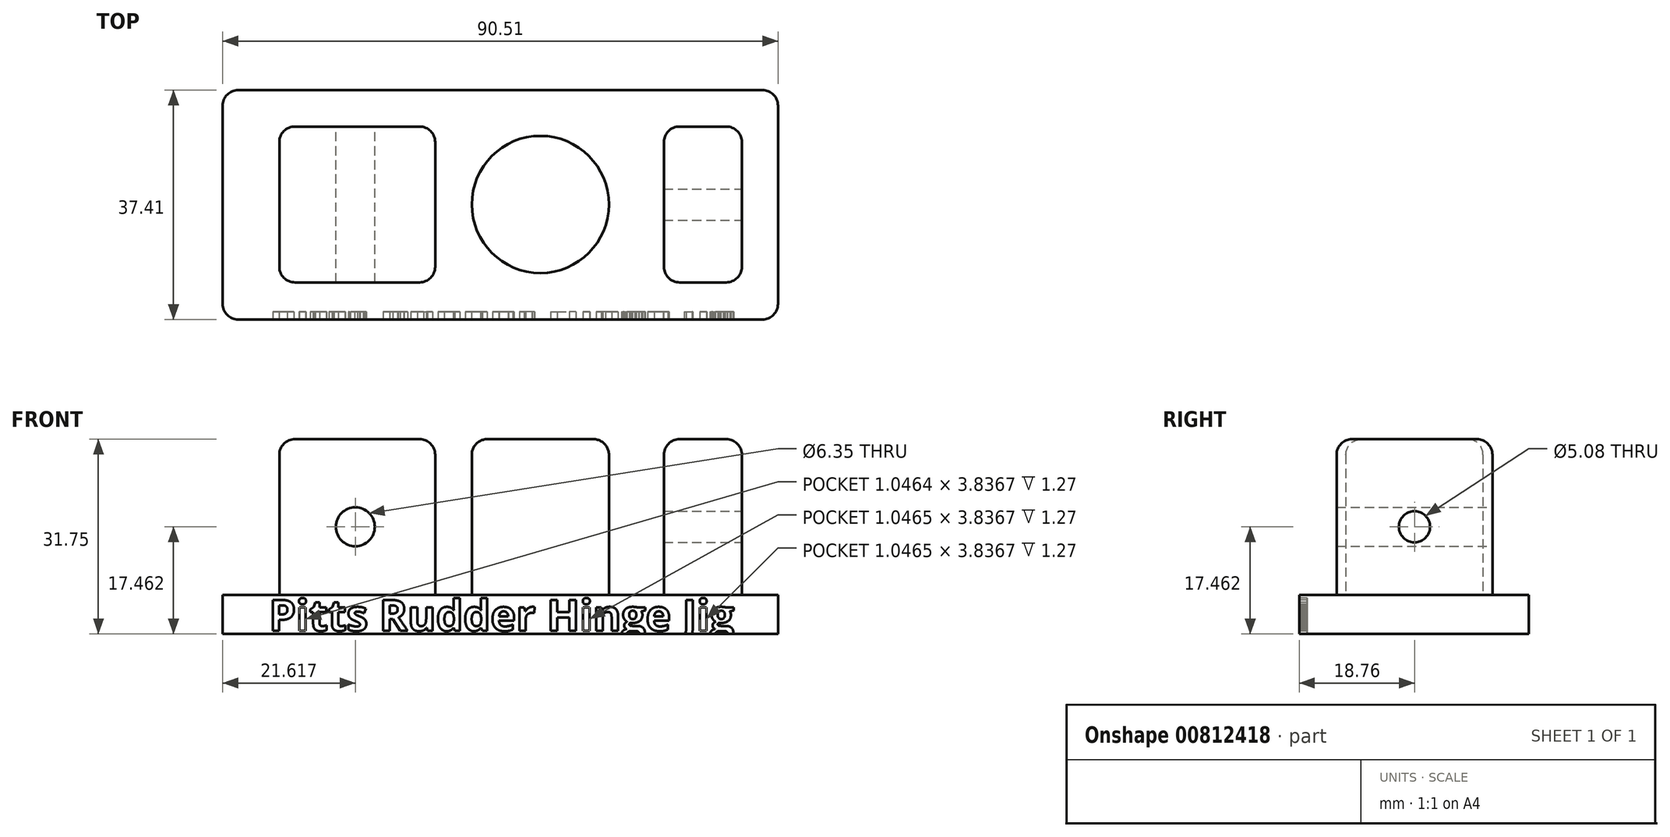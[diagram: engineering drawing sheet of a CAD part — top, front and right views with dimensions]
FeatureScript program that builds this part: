
annotation { "Feature Type Name" : "Feature", "Feature Type Description" : "" }
export const myFeature = defineFeature(function(context is Context, id is Id, definition is map)
    precondition{}
    {
        {
            var Q0;
            Q0=qCreatedBy(makeId("Top.planeOp"),FACE);
            var sketch = newSketch(context, id + "F0", { "sketchPlane" : qUnion([Q0])});
            skCircle(sketch, "E0", {"center": v(0, 0) * mm, "radius": 11.18 * mm});
            skLineSegment(sketch, "E1.bottom", {"start": v(-17.15, -12.7) * mm, "end": v(-42.55, -12.7) * mm});
            skLineSegment(sketch, "E1.top", {"start": v(-17.15, 12.7) * mm, "end": v(-42.55, 12.7) * mm});
            skLineSegment(sketch, "E1.left", {"start": v(-17.15, -12.7) * mm, "end": v(-17.15, 12.7) * mm});
            skLineSegment(sketch, "E1.right", {"start": v(-42.55, -12.7) * mm, "end": v(-42.55, 12.7) * mm});
            skPoint(sketch, "E1.middle", {"position": v(-29.85, 0) * mm});
            skLineSegment(sketch, "E2.bottom", {"start": v(32.85, -12.7) * mm, "end": v(20.15, -12.7) * mm});
            skLineSegment(sketch, "E2.top", {"start": v(32.85, 12.7) * mm, "end": v(20.15, 12.7) * mm});
            skLineSegment(sketch, "E2.left", {"start": v(32.85, -12.7) * mm, "end": v(32.85, 12.7) * mm});
            skLineSegment(sketch, "E2.right", {"start": v(20.15, -12.7) * mm, "end": v(20.15, 12.7) * mm});
            skPoint(sketch, "E2.middle", {"position": v(26.5, 0) * mm});
            skSolve(sketch);
        }
        {
            var Q0;
            Q0 = qSketchRegion(id + "F0", true);
            extrude(context, id + "F1", {"entities" : qUnion([Q0]), "depth" : 25.4 * mm, "offsetDistance" : 25.4 * mm});
        }
        {
            var Q0;
            Q0=qCreatedBy(makeId("Front.planeOp"),FACE);
            var sketch = newSketch(context, id + "F2", { "sketchPlane" : qUnion([Q0])});
            skCircle(sketch, "E3", {"center": v(-30.16, 11.11) * mm, "radius": 3.18 * mm});
            skSolve(sketch);
        }
        {
            var Q0;
            Q0 = qSketchRegion(id + "F2", true);
            extrude(context, id + "F3", {"entities" : qUnion([Q0]), "operationType" : NewBodyOperationType.REMOVE, "endBound" : BoundingType.SYMMETRIC, "depth" : 50.8 * mm, "offsetDistance" : 25.4 * mm});
        }
        {
            var Q0;
            Q0=makeQuery(id+"F1.opExtrude","SWEPT_FACE",FACE,{"disambiguationData":[OSD([sQuery(id+"F0.wireOp",EDGE,"E2.left")])]});
            var sketch = newSketch(context, id + "F4", { "sketchPlane" : qUnion([Q0])});
            skCircle(sketch, "E4", {"center": v(0, 11.11) * mm, "radius": 2.54 * mm});
            skSolve(sketch);
        }
        {
            var Q0;
            Q0 = qSketchRegion(id + "F4", true);
            extrude(context, id + "F5", {"entities" : qUnion([Q0]), "operationType" : NewBodyOperationType.REMOVE, "oppositeDirection" : true, "depth" : 15.24 * mm, "offsetDistance" : 25.4 * mm});
        }
        {
            var Q0;
            Q0=qCreatedBy(makeId("Top.planeOp"),FACE);
            var sketch = newSketch(context, id + "F6", { "sketchPlane" : qUnion([Q0])});
            skLineSegment(sketch, "E5.bottom", {"start": v(-51.78, 18.65) * mm, "end": v(38.73, 18.65) * mm});
            skLineSegment(sketch, "E5.top", {"start": v(-51.78, -18.76) * mm, "end": v(38.73, -18.76) * mm});
            skLineSegment(sketch, "E5.left", {"start": v(-51.78, 18.65) * mm, "end": v(-51.78, -18.76) * mm});
            skLineSegment(sketch, "E5.right", {"start": v(38.73, 18.65) * mm, "end": v(38.73, -18.76) * mm});
            skSolve(sketch);
        }
        {
            var Q0;
            Q0 = qSketchRegion(id + "F6", true);
            extrude(context, id + "F7", {"entities" : qUnion([Q0]), "oppositeDirection" : true, "depth" : 6.35 * mm, "offsetDistance" : 25.4 * mm});
        }
        {
            var Q0;
            Q0=makeQuery(id+"F1.opExtrude","SWEPT_EDGE",EDGE,{"disambiguationData":[OSD([sQuery(id+"F0.wireOp",EDGE,"E2.top"),sQuery(id+"F0.wireOp",EDGE,"E2.right")])]});
            var Q1;
            Q1=makeQuery(id+"F1.opExtrude","SWEPT_EDGE",EDGE,{"disambiguationData":[OSD([sQuery(id+"F0.wireOp",EDGE,"E2.top"),sQuery(id+"F0.wireOp",EDGE,"E2.left")])]});
            var Q2;
            Q2=makeQuery(id+"F1.opExtrude","SWEPT_EDGE",EDGE,{"disambiguationData":[OSD([sQuery(id+"F0.wireOp",EDGE,"E2.bottom"),sQuery(id+"F0.wireOp",EDGE,"E2.right")])]});
            var Q3;
            Q3=makeQuery(id+"F1.opExtrude","SWEPT_EDGE",EDGE,{"disambiguationData":[OSD([sQuery(id+"F0.wireOp",EDGE,"E1.top"),sQuery(id+"F0.wireOp",EDGE,"E1.left")])]});
            var Q4;
            Q4=makeQuery(id+"F1.opExtrude","SWEPT_EDGE",EDGE,{"disambiguationData":[OSD([sQuery(id+"F0.wireOp",EDGE,"E1.top"),sQuery(id+"F0.wireOp",EDGE,"E1.right")])]});
            var Q5;
            Q5=makeQuery(id+"F1.opExtrude","SWEPT_EDGE",EDGE,{"disambiguationData":[OSD([sQuery(id+"F0.wireOp",EDGE,"E1.bottom"),sQuery(id+"F0.wireOp",EDGE,"E1.right")])]});
            var Q6;
            Q6=makeQuery(id+"F1.opExtrude","SWEPT_EDGE",EDGE,{"disambiguationData":[OSD([sQuery(id+"F0.wireOp",EDGE,"E2.bottom"),sQuery(id+"F0.wireOp",EDGE,"E2.left")])]});
            var Q7;
            Q7=makeQuery(id+"F1.opExtrude","SWEPT_EDGE",EDGE,{"disambiguationData":[OSD([sQuery(id+"F0.wireOp",EDGE,"E1.bottom"),sQuery(id+"F0.wireOp",EDGE,"E1.left")])]});
            var Q8;
            Q8=makeQuery(id+"F7.opExtrude","SWEPT_EDGE",EDGE,{"disambiguationData":[OSD([sQuery(id+"F6.wireOp",EDGE,"E5.top"),sQuery(id+"F6.wireOp",EDGE,"E5.left")])]});
            var Q9;
            Q9=makeQuery(id+"F7.opExtrude","SWEPT_EDGE",EDGE,{"disambiguationData":[OSD([sQuery(id+"F6.wireOp",EDGE,"E5.bottom"),sQuery(id+"F6.wireOp",EDGE,"E5.left")])]});
            var Q10;
            Q10=makeQuery(id+"F7.opExtrude","SWEPT_EDGE",EDGE,{"disambiguationData":[OSD([sQuery(id+"F6.wireOp",EDGE,"E5.top"),sQuery(id+"F6.wireOp",EDGE,"E5.right")])]});
            var Q11;
            Q11=makeQuery(id+"F7.opExtrude","SWEPT_EDGE",EDGE,{"disambiguationData":[OSD([sQuery(id+"F6.wireOp",EDGE,"E5.bottom"),sQuery(id+"F6.wireOp",EDGE,"E5.right")])]});
            var Q12;
            Q12=makeQuery(id+"F1.opExtrude","CAP_EDGE",EDGE,{"disambiguationData":[OSD([sQuery(id+"F0.wireOp",EDGE,"E1.top")])],"isStart":false});
            var Q13;
            Q13=makeQuery(id+"F1.opExtrude","CAP_EDGE",EDGE,{"disambiguationData":[OSD([sQuery(id+"F0.wireOp",EDGE,"E1.left")])],"isStart":false});
            var Q14;
            Q14=makeQuery(id+"F1.opExtrude","CAP_EDGE",EDGE,{"disambiguationData":[OSD([sQuery(id+"F0.wireOp",EDGE,"E1.bottom")])],"isStart":false});
            var Q15;
            Q15=makeQuery(id+"F1.opExtrude","CAP_EDGE",EDGE,{"disambiguationData":[OSD([sQuery(id+"F0.wireOp",EDGE,"E1.right")])],"isStart":false});
            var Q16;
            Q16=makeQuery(id+"F1.opExtrude","CAP_EDGE",EDGE,{"disambiguationData":[OSD([sQuery(id+"F0.wireOp",EDGE,"E2.bottom")])],"isStart":false});
            var Q17;
            Q17=makeQuery(id+"F1.opExtrude","CAP_EDGE",EDGE,{"disambiguationData":[OSD([sQuery(id+"F0.wireOp",EDGE,"E2.top")])],"isStart":false});
            var Q18;
            Q18=makeQuery(id+"F1.opExtrude","CAP_EDGE",EDGE,{"disambiguationData":[OSD([sQuery(id+"F0.wireOp",EDGE,"E2.right")])],"isStart":false});
            var Q19;
            Q19=makeQuery(id+"F1.opExtrude","CAP_EDGE",EDGE,{"disambiguationData":[OSD([sQuery(id+"F0.wireOp",EDGE,"E2.left")])],"isStart":false});
            var Q20;
            Q20=makeQuery(id+"F1.opExtrude","CAP_EDGE",EDGE,{"disambiguationData":[OSD([sQuery(id+"F0.wireOp",EDGE,"E0")])],"isStart":false});
            fillet(context, id + "F8", {"entities" : qUnion([Q0, Q1, Q2, Q3, Q4, Q5, Q6, Q7, Q8, Q9, Q10, Q11, Q12, Q13, Q14, Q15, Q16, Q17, Q18, Q19, Q20]), "radius" : 2.54 * mm, "tangentPropagation" : true, "allowEdgeOverflow" : false});
        }
        {
            var Q0;
            Q0=makeQuery(id+"F7.opExtrude","SWEPT_FACE",FACE,{"disambiguationData":[OSD([sQuery(id+"F6.wireOp",EDGE,"E5.top")])]});
            var sketch = newSketch(context, id + "F9", { "sketchPlane" : qUnion([Q0])});
            skText(sketch, "E6", { "text": "Pitts Rudder Hinge Jig", "fontName": "OpenSans-Bold.ttf"});
            const initialGuessF9  = {"E6": [-0.04425, -0.00584, 1, 0, 0.00506]};
            skSetInitialGuess(sketch, initialGuessF9);
            skSolve(sketch);
        }
        {
            var Q0;
            Q0 = qSketchRegion(id + "F9", true);
            extrude(context, id + "F10", {"entities" : qUnion([Q0]), "operationType" : NewBodyOperationType.REMOVE, "oppositeDirection" : true, "depth" : 1.27 * mm, "offsetDistance" : 25.4 * mm});
        }
    });
